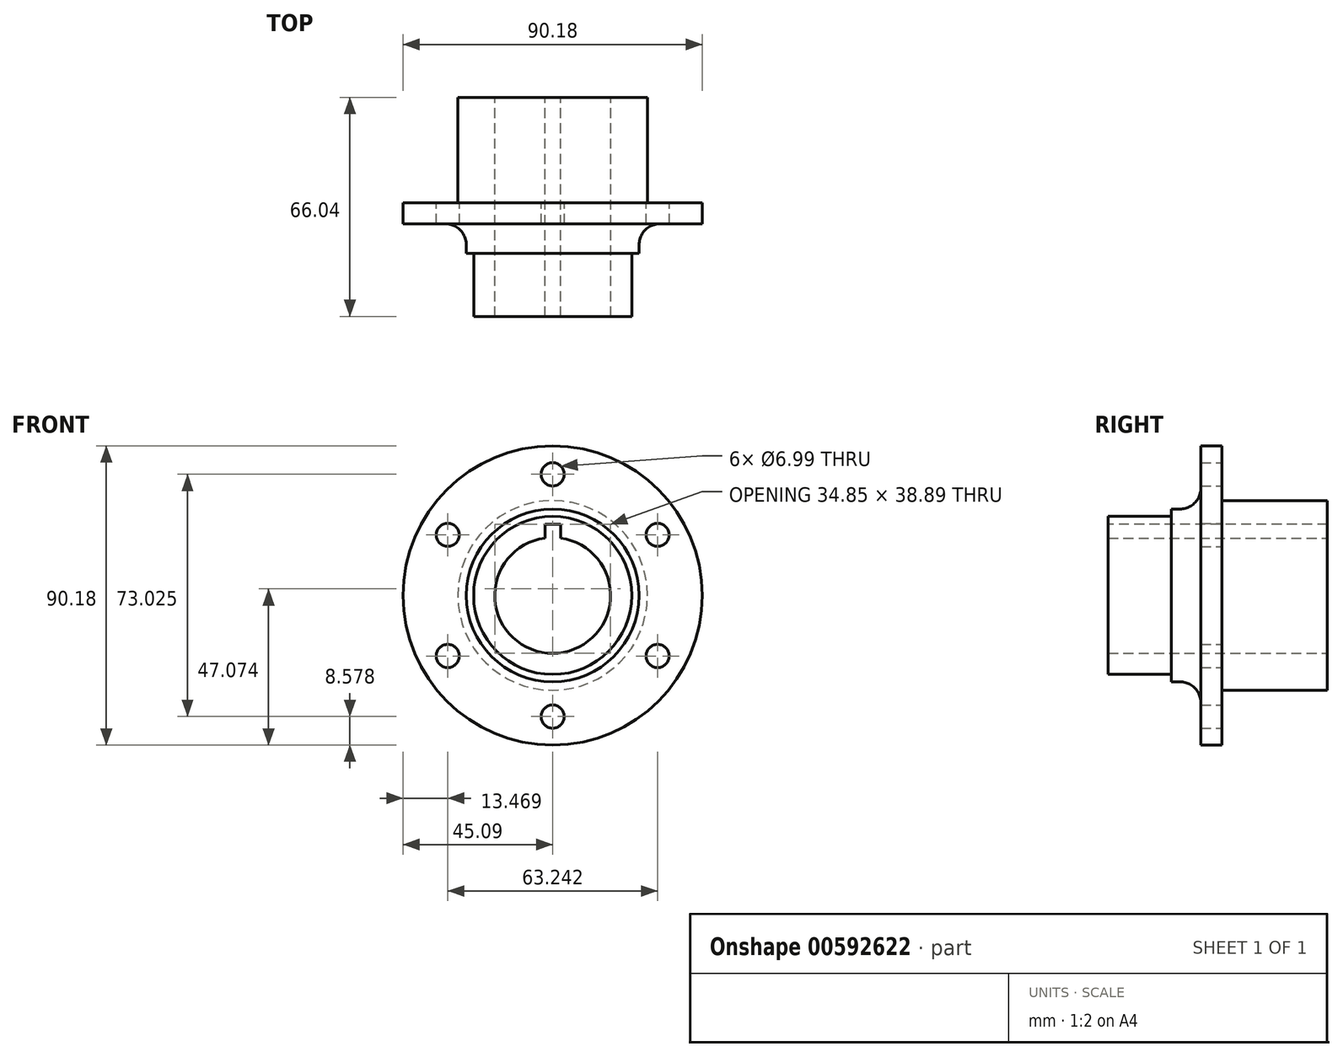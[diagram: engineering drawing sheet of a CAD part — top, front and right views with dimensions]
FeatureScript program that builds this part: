
annotation { "Feature Type Name" : "Feature", "Feature Type Description" : "" }
export const myFeature = defineFeature(function(context is Context, id is Id, definition is map)
    precondition{}
    {
        {
            var Q0;
            Q0=qCreatedBy(makeId("Right.planeOp"),FACE);
            var sketch = newSketch(context, id + "F0", { "sketchPlane" : qUnion([Q0])});
            skLineSegment(sketch, "E0", {"start": v(0, 0) * mm, "end": v(66.04, 0) * mm});
            skLineSegment(sketch, "E1", {"start": v(0, 0) * mm, "end": v(0, 23.81) * mm});
            skLineSegment(sketch, "E2", {"start": v(0, 23.81) * mm, "end": v(19.05, 23.81) * mm});
            skLineSegment(sketch, "E3", {"start": v(19.05, 23.81) * mm, "end": v(19.05, 26.04) * mm});
            skLineSegment(sketch, "E4", {"start": v(19.05, 26.04) * mm, "end": v(21.59, 26.04) * mm});
            skLineSegment(sketch, "E5", {"start": v(27.94, 32.39) * mm, "end": v(27.94, 45.09) * mm});
            skLineSegment(sketch, "E6", {"start": v(27.94, 45.09) * mm, "end": v(34.3, 45.09) * mm});
            skLineSegment(sketch, "E7", {"start": v(34.3, 45.09) * mm, "end": v(34.3, 28.57) * mm});
            skLineSegment(sketch, "E8", {"start": v(34.3, 28.57) * mm, "end": v(66.04, 28.57) * mm});
            skLineSegment(sketch, "E9", {"start": v(66.04, 28.57) * mm, "end": v(66.04, 0) * mm});
            skPoint(sketch, "E10.visualSharp", {"position": v(27.94, 26.04) * mm});
            skArc(sketch, "E10.filletArc", {"start": v(21.59, 26.04) * mm, "mid": v(26.08, 27.9) * mm, "end": v(27.94, 32.39) * mm});
            skSolve(sketch);
        }
        {
            var Q0;
            Q0=qCreatedBy(makeId("Right.planeOp"),FACE);
            var sketch = newSketch(context, id + "F1", { "sketchPlane" : qUnion([Q0])});
            skLineSegment(sketch, "E11", {"start": v(0, 0) * mm, "end": v(76.2, 0) * mm});
            skSolve(sketch);
        }
        {
            var Q0;
            Q0 = qSketchRegion(id + "F1", true);
            var Q1;
            Q1=makeQuery(id+"F0.imprint","IMPRINT",FACE,{"disambiguationData":[TD([[makeQuery(id+"F0.imprint","IMPRINT",EDGE,{"derivedFrom":sQuery(id+"F0.wireOp",EDGE,"E0")}),1.0]])]});
            var Q2;
            Q2=sQuery(id+"F1.wireOp",EDGE,"E11");
            revolve(context, id + "F2", {"entities" : qUnion([Q0, Q1]), "axis" : qUnion([Q2]), "revolveType" : RevolveType.FULL});
        }
        {
            var Q0;
            Q0=makeQuery(id+"F2.opRevolve","SWEPT_FACE",FACE,{"disambiguationData":[OSD([sQuery(id+"F0.wireOp",EDGE,"E1")])]});
            var sketch = newSketch(context, id + "F3", { "sketchPlane" : qUnion([Q0])});
            skCircle(sketch, "E12", {"center": v(0, 0) * mm, "radius": 17.46 * mm});
            skSolve(sketch);
        }
        {
            var Q0;
            Q0=sQuery(id+"F3.wireOp",VERTEX,"E12.center");
            var Q1;
            Q1=makeQuery(id+"F2.opRevolve","SWEPT_BODY",BODY,{"disambiguationData":[OSD([sQuery(id+"F0.wireOp",EDGE,"E0"),sQuery(id+"F0.wireOp",EDGE,"E1"),sQuery(id+"F0.wireOp",EDGE,"E2"),sQuery(id+"F0.wireOp",EDGE,"E3"),sQuery(id+"F0.wireOp",EDGE,"E4"),sQuery(id+"F0.wireOp",EDGE,"E5"),sQuery(id+"F0.wireOp",EDGE,"E6"),sQuery(id+"F0.wireOp",EDGE,"E7"),sQuery(id+"F0.wireOp",EDGE,"E8"),sQuery(id+"F0.wireOp",EDGE,"E9"),sQuery(id+"F0.wireOp",EDGE,"E10.filletArc")])]});
            hole(context, id + "F4", {"style" : HoleStyle.SIMPLE, "endStyle" : HoleEndStyle.THROUGH, "holeDiameter" : 34.92 * mm, "majorDiameter" : 6.35 * mm, "isTappedThrough" : true, "tappedDepth" : 12.7 * mm, "tapClearance" : 3, "startFromSketch" : true, "locations" : qUnion([Q0]), "scope" : qUnion([Q1])});
        }
        {
            var Q0;
            Q0=makeQuery(id+"F2.opRevolve","SWEPT_FACE",FACE,{"disambiguationData":[OSD([sQuery(id+"F0.wireOp",EDGE,"E5")])]});
            var sketch = newSketch(context, id + "F5", { "sketchPlane" : qUnion([Q0])});
            skCircle(sketch, "E13", {"center": v(0, 0) * mm, "radius": 36.51 * mm});
            skLineSegment(sketch, "E14", {"start": v(0, 0) * mm, "end": v(0, 36.51) * mm});
            skCircle(sketch, "E15", {"center": v(0, 36.51) * mm, "radius": 3.5 * mm});
            skCircle(sketch, "E16.1.0", {"center": v(-31.62, 18.26) * mm, "radius": 3.5 * mm});
            skCircle(sketch, "E16.2.0", {"center": v(-31.62, -18.26) * mm, "radius": 3.5 * mm});
            skCircle(sketch, "E16.3.0", {"center": v(0, -36.51) * mm, "radius": 3.5 * mm});
            skCircle(sketch, "E16.4.0", {"center": v(31.62, -18.26) * mm, "radius": 3.5 * mm});
            skCircle(sketch, "E16.5.0", {"center": v(31.62, 18.26) * mm, "radius": 3.5 * mm});
            skSolve(sketch);
        }
        {
            var Q0;
            Q0=sQuery(id+"F5.wireOp",VERTEX,"E14.end");
            var Q1;
            Q1=sQuery(id+"F5.wireOp",VERTEX,"E16.5.0.center");
            var Q2;
            Q2=sQuery(id+"F5.wireOp",VERTEX,"E16.4.0.center");
            var Q3;
            Q3=sQuery(id+"F5.wireOp",VERTEX,"E16.3.0.center");
            var Q4;
            Q4=sQuery(id+"F5.wireOp",VERTEX,"E16.2.0.center");
            var Q5;
            Q5=sQuery(id+"F5.wireOp",VERTEX,"E16.1.0.center");
            var Q6;
            Q6=makeQuery(id+"F2.opRevolve","SWEPT_BODY",BODY,{"disambiguationData":[OSD([sQuery(id+"F0.wireOp",EDGE,"E0"),sQuery(id+"F0.wireOp",EDGE,"E1"),sQuery(id+"F0.wireOp",EDGE,"E2"),sQuery(id+"F0.wireOp",EDGE,"E3"),sQuery(id+"F0.wireOp",EDGE,"E4"),sQuery(id+"F0.wireOp",EDGE,"E5"),sQuery(id+"F0.wireOp",EDGE,"E6"),sQuery(id+"F0.wireOp",EDGE,"E7"),sQuery(id+"F0.wireOp",EDGE,"E8"),sQuery(id+"F0.wireOp",EDGE,"E9"),sQuery(id+"F0.wireOp",EDGE,"E10.filletArc")])]});
            hole(context, id + "F6", {"style" : HoleStyle.SIMPLE, "endStyle" : HoleEndStyle.THROUGH, "holeDiameter" : 7 * mm, "majorDiameter" : 6.35 * mm, "isTappedThrough" : true, "tappedDepth" : 12.7 * mm, "tapClearance" : 3, "startFromSketch" : true, "locations" : qUnion([Q0, Q1, Q2, Q3, Q4, Q5]), "scope" : qUnion([Q6])});
        }
        {
            var Q0;
            Q0=qCreatedBy(makeId("Front.planeOp"),FACE);
            var sketch = newSketch(context, id + "F7", { "sketchPlane" : qUnion([Q0])});
            skLineSegment(sketch, "E17", {"start": v(0, 0) * mm, "end": v(0, 16.8) * mm});
            skLineSegment(sketch, "E18", {"start": v(0, 21.43) * mm, "end": v(2.35, 21.43) * mm});
            skLineSegment(sketch, "E19", {"start": v(2.35, 21.43) * mm, "end": v(2.35, 16.8) * mm});
            skLineSegment(sketch, "E20", {"start": v(2.35, 16.8) * mm, "end": v(-2.35, 16.8) * mm});
            skLineSegment(sketch, "E21", {"start": v(-2.35, 16.8) * mm, "end": v(-2.35, 21.43) * mm});
            skLineSegment(sketch, "E22", {"start": v(0, 21.43) * mm, "end": v(-2.35, 21.43) * mm});
            skSolve(sketch);
        }
        {
            var Q0;
            Q0=makeQuery(id+"F7.imprint","IMPRINT",FACE,{"disambiguationData":[TD([[makeQuery(id+"F7.imprint","IMPRINT",EDGE,{"derivedFrom":sQuery(id+"F7.wireOp",EDGE,"E18")}),-1.0]])]});
            extrude(context, id + "F8", {"entities" : qUnion([Q0]), "operationType" : NewBodyOperationType.REMOVE, "oppositeDirection" : true, "depth" : 66.04 * mm, "offsetDistance" : 25.4 * mm});
        }
    });
